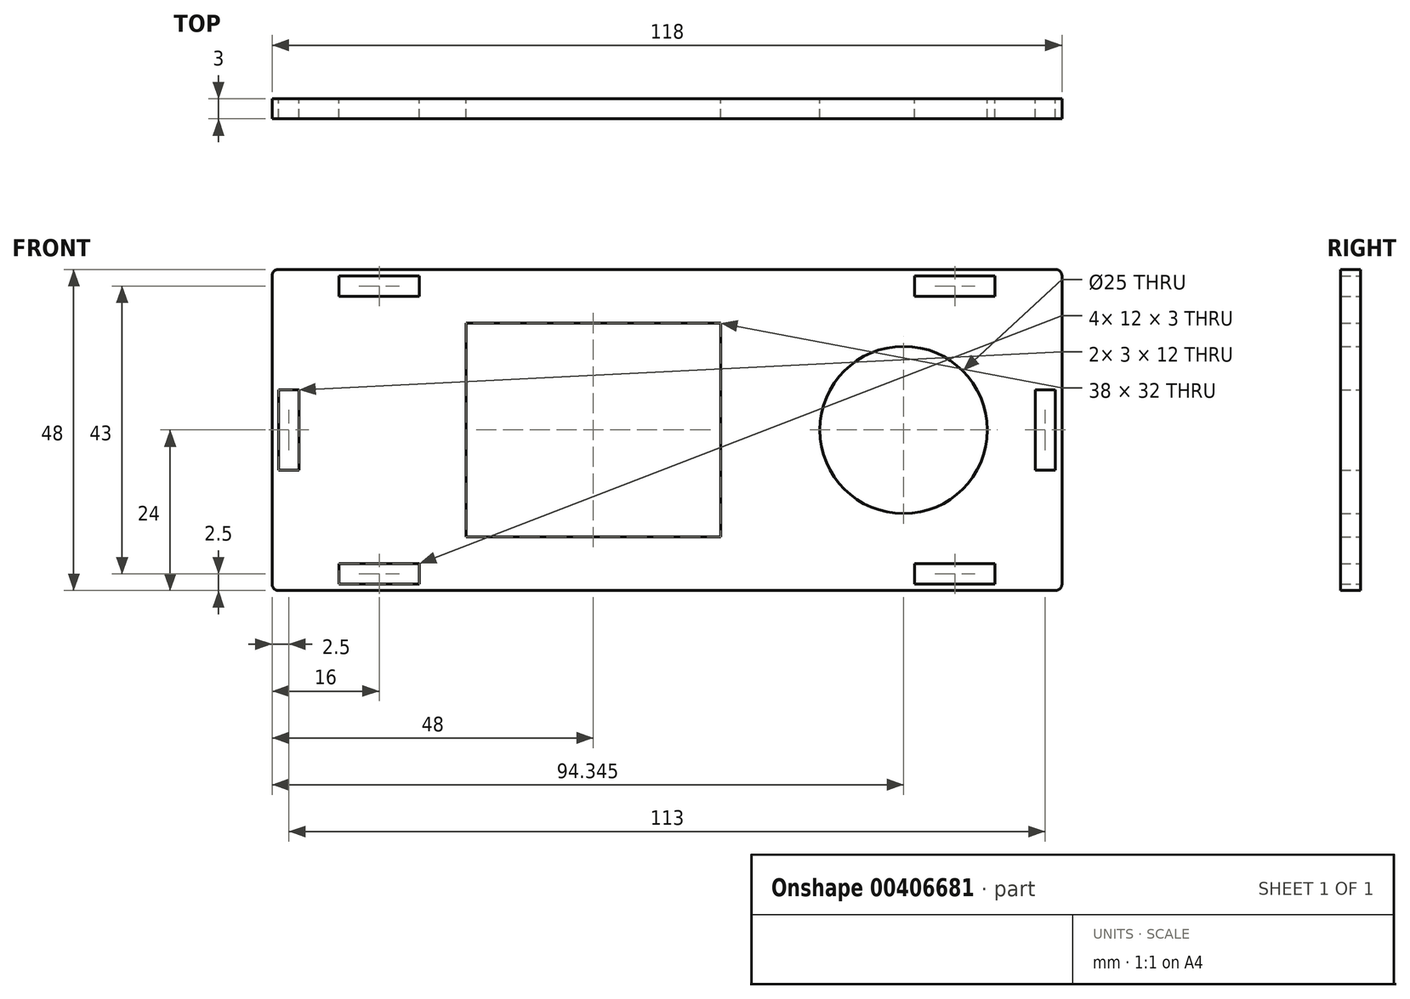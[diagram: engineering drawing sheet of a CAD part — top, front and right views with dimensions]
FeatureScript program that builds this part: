
annotation { "Feature Type Name" : "Feature", "Feature Type Description" : "" }
export const myFeature = defineFeature(function(context is Context, id is Id, definition is map)
    precondition{}
    {
        {
            var Q0;
            Q0=qCreatedBy(makeId("Front.planeOp"),FACE);
            var sketch = newSketch(context, id + "F0", { "sketchPlane" : qUnion([Q0])});
            skLineSegment(sketch, "E0.bottom", {"start": v(-54, 19) * mm, "end": v(54, 19) * mm});
            skLineSegment(sketch, "E0.top", {"start": v(-54, -19) * mm, "end": v(54, -19) * mm});
            skLineSegment(sketch, "E0.left", {"start": v(-54, 19) * mm, "end": v(-54, -19) * mm});
            skLineSegment(sketch, "E0.right", {"start": v(54, 19) * mm, "end": v(54, -19) * mm});
            skPoint(sketch, "E0.middle", {"position": v(0, 0) * mm});
            skPoint(sketch, "E1.visualSharp", {"position": v(-54, 19) * mm});
            skPoint(sketch, "E2.visualSharp", {"position": v(54, -19) * mm});
            skPoint(sketch, "E3.visualSharp", {"position": v(54, 19) * mm});
            skPoint(sketch, "E4.visualSharp", {"position": v(-54, -19) * mm});
            skLineSegment(sketch, "E5.1", {"start": v(-59, 23) * mm, "end": v(-59, -23) * mm});
            skLineSegment(sketch, "E5.2", {"start": v(-58, 24) * mm, "end": v(58, 24) * mm});
            skLineSegment(sketch, "E5.5", {"start": v(59, 23) * mm, "end": v(59, -23) * mm});
            skLineSegment(sketch, "E5.7", {"start": v(-58, -24) * mm, "end": v(58, -24) * mm});
            skLineSegment(sketch, "E6.bottom", {"start": v(-49, 20) * mm, "end": v(-37, 20) * mm});
            skLineSegment(sketch, "E6.top", {"start": v(-49, 23) * mm, "end": v(-37, 23) * mm});
            skLineSegment(sketch, "E6.left", {"start": v(-49, 20) * mm, "end": v(-49, 23) * mm});
            skLineSegment(sketch, "E6.right", {"start": v(-37, 20) * mm, "end": v(-37, 23) * mm});
            skLineSegment(sketch, "E7.bottom", {"start": v(49, 23) * mm, "end": v(37, 23) * mm});
            skLineSegment(sketch, "E7.top", {"start": v(49, 20) * mm, "end": v(37, 20) * mm});
            skLineSegment(sketch, "E7.left", {"start": v(49, 23) * mm, "end": v(49, 20) * mm});
            skLineSegment(sketch, "E7.right", {"start": v(37, 23) * mm, "end": v(37, 20) * mm});
            skLineSegment(sketch, "E8.bottom", {"start": v(49, -20) * mm, "end": v(37, -20) * mm});
            skLineSegment(sketch, "E8.top", {"start": v(49, -23) * mm, "end": v(37, -23) * mm});
            skLineSegment(sketch, "E8.left", {"start": v(49, -20) * mm, "end": v(49, -23) * mm});
            skLineSegment(sketch, "E8.right", {"start": v(37, -20) * mm, "end": v(37, -23) * mm});
            skLineSegment(sketch, "E9.bottom", {"start": v(-49, -20) * mm, "end": v(-37, -20) * mm});
            skLineSegment(sketch, "E9.top", {"start": v(-49, -23) * mm, "end": v(-37, -23) * mm});
            skLineSegment(sketch, "E9.left", {"start": v(-49, -20) * mm, "end": v(-49, -23) * mm});
            skLineSegment(sketch, "E9.right", {"start": v(-37, -20) * mm, "end": v(-37, -23) * mm});
            skLineSegment(sketch, "E10.bottom", {"start": v(-58, 6) * mm, "end": v(-55, 6) * mm});
            skLineSegment(sketch, "E10.top", {"start": v(-58, -6) * mm, "end": v(-55, -6) * mm});
            skLineSegment(sketch, "E10.left", {"start": v(-58, 6) * mm, "end": v(-58, -6) * mm});
            skLineSegment(sketch, "E10.right", {"start": v(-55, 6) * mm, "end": v(-55, -6) * mm});
            skLineSegment(sketch, "E11.bottom", {"start": v(55, 6) * mm, "end": v(58, 6) * mm});
            skLineSegment(sketch, "E11.top", {"start": v(55, -6) * mm, "end": v(58, -6) * mm});
            skLineSegment(sketch, "E11.left", {"start": v(55, 6) * mm, "end": v(55, -6) * mm});
            skLineSegment(sketch, "E11.right", {"start": v(58, 6) * mm, "end": v(58, -6) * mm});
            skCircle(sketch, "E12", {"center": v(35.34, 0) * mm, "radius": 12.5 * mm});
            skLineSegment(sketch, "E13.bottom", {"start": v(-30, 16) * mm, "end": v(8, 16) * mm});
            skLineSegment(sketch, "E13.top", {"start": v(-30, -16) * mm, "end": v(8, -16) * mm});
            skLineSegment(sketch, "E13.left", {"start": v(-30, 16) * mm, "end": v(-30, -16) * mm});
            skLineSegment(sketch, "E13.right", {"start": v(8, 16) * mm, "end": v(8, -16) * mm});
            skLineSegment(sketch, "E14", {"start": v(0, 0) * mm, "end": v(-4.61, 0) * mm, "construction": true});
            skPoint(sketch, "E15.visualSharp", {"position": v(-59, 24) * mm});
            skArc(sketch, "E15.filletArc", {"start": v(-58, 24) * mm, "mid": v(-58.7, 23.7) * mm, "end": v(-59, 23) * mm});
            skArc(sketch, "E16.MirrorCS", {"start": v(58, 24) * mm, "mid": v(58.7, 23.7) * mm, "end": v(59, 23) * mm});
            skArc(sketch, "E17.MirrorCS", {"start": v(-58, -24) * mm, "mid": v(-58.7, -23.7) * mm, "end": v(-59, -23) * mm});
            skArc(sketch, "E18.MirrorCS", {"start": v(58, -24) * mm, "mid": v(58.7, -23.7) * mm, "end": v(59, -23) * mm});
            skPoint(sketch, "E19.orphan", {"position": v(59, 24) * mm});
            skPoint(sketch, "E20.orphan", {"position": v(59, -24) * mm});
            skPoint(sketch, "E21.orphan", {"position": v(-59, -24) * mm});
            skSolve(sketch);
        }
        {
            var Q0;
            Q0=makeQuery(id+"F0.imprint","IMPRINT",FACE,{"disambiguationData":[TD([[makeQuery(id+"F0.imprint","IMPRINT",EDGE,{"derivedFrom":sQuery(id+"F0.wireOp",EDGE,"E0.bottom")}),1.0]])]});
            var Q1;
            Q1=makeQuery(id+"F0.imprint","IMPRINT",FACE,{"disambiguationData":[TD([[makeQuery(id+"F0.imprint","IMPRINT",EDGE,{"derivedFrom":sQuery(id+"F0.wireOp",EDGE,"E0.bottom")}),-1.0]])]});
            extrude(context, id + "F1", {"entities" : qUnion([Q0, Q1]), "depth" : 3 * mm});
        }
    });
